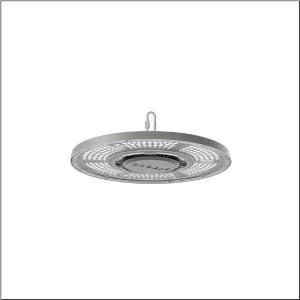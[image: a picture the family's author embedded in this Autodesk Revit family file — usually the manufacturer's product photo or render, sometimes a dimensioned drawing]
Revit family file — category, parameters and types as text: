
# Revit family: highbay_31-s_51hc427a4fmb
name_source: partatom
category: Lighting Fixtures
units: mm (PartAtom-declared; Revit-internal decimal feet)

## family parameters
Cut with Voids When Loaded = No
Host = Face
Light Source = No
Part Type = Normal
Room Calculation Point = No
Round Connector Dimension = Use Diameter
Shared = No

## types (1)
- Highbay 31-S (1 x LED, 14000 lm, 94 W, 4000K)
    Apparent Load = 94 VA
    CIE Flux Codes = 77 99 100 100 100
    Color Rendering = 80
    Color Temperature = 4000K
    Default Elevation = 1800 mm
    Description = Highbay 31-S, LED high bay luminaire, primary light control with lens, of PC, primary optical cover: cover panel, of PC, transparent, light emission: direct distribution, primary light characteristic: rotationally symmetric, installation type: suspended mounting, surface-mounted, LED, rated luminous flux: 14.000lm, luminous efficacy: 150lm/W, light colour: 840, colour temperature: 4000K, control gear: ECG, with cable, 3x 1.0mm², free wire ends, mains connection: 220..240V, AC/DC, 0/50..60Hz, cable length: 1,5m, rated input power: 94W, housing, rotationally symmetric, of diecast aluminium, powder-coated, grey aluminium (RAL 9007), with hook on luminaire side, incl. screw, diameter: 339mm, protection rating (complete): IP65, insulation class (complete): insulation class I (protective earthing), certification: CE, ENEC, UKCA, protection symbol: D, impact resistance: IK08, permissible operating ambient temperature: -30..+45°C, standard: EN 60598-2-22, EN 60598, corresponds to IFS (International Featured Standards) requirements for safety and quality in the food industry, packaging unit: 1 piece
    Height = 141 mm
    Lamp = 1 x LED
    Lamp Light Flux = 14000 lm
    Lamp Power = 94 W
    Lamp count = 1
    Length = 339 mm
    Luminous efficacy = 149 lm/W
    Manufacturer = Siteco
    ModVariant = No
    Model = 51HC427A4FMB
    Mounting Place = Ceiling
    Mounting Type = Pendant
    Number of Poles = 1
    OnlyDefault = Yes
    Power Factor = 1
    Product Name = Highbay 31-S
    Product group = LED high bay luminaire
    ProductGroupID = 903
    Protection Class = Protection class I
    Protection Degree = IP 65
    RLX_Detail_Level = 1
    RLX_Emergency_Light_Flux = 0 lm
    RLX_Emergency_Type = 0
    RLX_Emergency_Type_DB = No
    RlxData = <blob elided: 164029 chars, md5=d2c5a7df>
    Socket = socket
    Standby Power = 0 W
    System Light Flux = 14000 lm
    System Power = 94 W
    Type Comments = Product without accessories
    Type Image = l_1007237.jpg
    URL = http://relux.com
    VarID = ---
    Voltage = 0 V
    Weight = 0.00 kg
    Width = 0 mm  [stored 0 ft]

note: [stored X ft] marks values corroborated as IEEE doubles in the binary element streams (Revit-internal decimal feet)

## geometry (parser evidence)
native form markers: Blend x4, Sweep x8
no freeform markers — native parametric forms only
